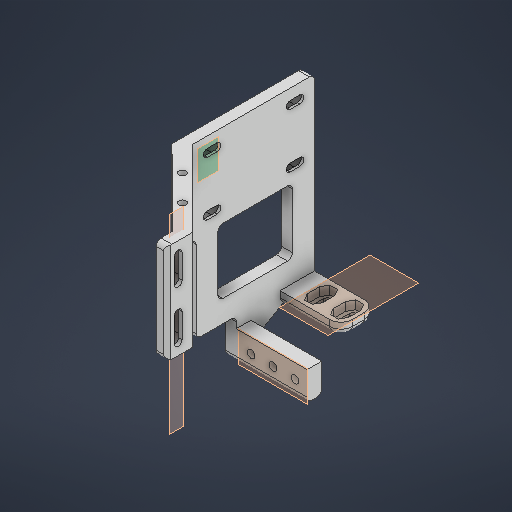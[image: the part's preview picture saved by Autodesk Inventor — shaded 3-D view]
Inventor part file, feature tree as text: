
AUTODESK INVENTOR PART (.ipt)
format: ipt  version: 2025 (Build 290162000, 162)  size: 845,824 bytes
history: native  units: mm
features: reference x38, extrude x24, sketch x21, other x9, plane x7, fillet x7, projected_geometry x5, chamfer x3, loft x1
ambient origin geometry x8: Origin, YZ Plane, XZ Plane, XY Plane, X Axis, Y Axis, Z Axis, Center Point
bodies: Solid1 (feature_tree)
feature tree (115):
  plane  "Work Plane1"
  extrude  "Extrusion1"  Depth=4.5mm TaperAngle=0.0deg
  plane  "Work Plane2"
  extrude  "Extrusion2"  Depth=2.0mm
  extrude  "Extrusion4"  Depth=3.2mm
  extrude  "Extrusion5"  Depth=6.0mm
  sketch  "Sketch7"  dims[d22=6.0mm d23=6.0mm]
  plane  "Work Plane3"
  extrude  "Extrusion6"  Depth=6.0mm
  plane  "Work Plane4"
  extrude  "Extrusion7"  Depth=6.0mm TaperAngle=0.0deg
  extrude  "Extrusion8"  Depth=6.0mm
  sketch  "Sketch10"  dims[d31=6.0mm d32=6.0mm]
  plane  "Work Plane5"
  extrude  "Extrusion9"  Depth=6.0mm
  extrude  "Extrusion10"  Depth=4.5mm
  loft  "Loft3"
  extrude  "Extrusion11"  Depth=10.58mm
  extrude  "Extrusion12"  Depth=3.0mm
  extrude  "Extrusion13"  Depth=4.5mm TaperAngle=0.0deg
  sketch  "Sketch15"  dims[d51=4.5mm d52=0.0mm d53=4.5mm d54=0.0mm]
  plane  "Work Plane6"
  extrude  "Extrusion14"  Depth=10.0mm
  fillet  "Fillet3"  Radius=24.197245mm
  sketch  "Sketch16"  dims[d55=10.0mm d56=0.0mm d57=7.218682mm d58=24.197245mm]
  extrude  "Extrusion15"  TaperAngle=0.0deg  [1 undecoded]
  extrude  "Extrusion16"  Depth=1.893mm
  extrude  "Extrusion17"  Depth=10.0mm TaperAngle=0.0deg
  extrude  "Extrusion18"  Depth=3.2mm
  chamfer  "Chamfer2"  Distance=3.2mm
  chamfer  "Chamfer3"  Distance=6.0mm
  fillet  "Fillet4"  Radius=6.0mm
  extrude  "Extrusion20"  Depth=6.0mm
  chamfer  "Chamfer4"  Distance=6.0mm
  sketch  "Sketch20"  dims[d66=10.0mm d67=0.0mm d68=10.0mm d69=0.0mm]
  extrude  "Extrusion21"  Depth=6.0mm
  extrude  "Extrusion22"  Depth=6.0mm
  fillet  "Fillet5"  Radius=3.0mm
  extrude  "Extrusion23"  Depth=10.0mm TaperAngle=0.0deg
  extrude  "Extrusion24"  Depth=9.0mm
  fillet  "Fillet6"  Radius=2.0mm
  fillet  "Fillet7"  Radius=1.5mm
  plane  "Work Plane8"
  extrude  "Extrusion27"  Depth=2.0mm
  extrude  "Extrusion28"  Depth=10.0mm
  fillet  "Fillet11"  Radius=3.2mm
  fillet  "Fillet12"  Radius=10.0mm
  sketch  "Sketch1"  dims[d0=4.5mm d1=0.0mm d2=4.5mm d3=0.0mm]
  reference  "Reference1"
  reference  "Reference2"
  reference  "Reference3"
  reference  "Reference4"
  reference  "Reference5"
  reference  "Reference6"
  reference  "Reference7"
  reference  "Reference8"
  reference  "Reference9"
  reference  "Reference10"
  reference  "Reference11"
  reference  "Reference12"
  reference  "Reference13"
  reference  "Reference14"
  reference  "Reference15"
  reference  "Reference16"
  reference  "Reference17"
  reference  "Reference18"
  reference  "Reference19"
  reference  "Reference20"
  sketch  "Sketch2"  dims[d8=2.0mm d17=3.2mm]
  reference  "Reference21"
  reference  "Reference22"
  reference  "Reference23"
  reference  "Reference24"
  reference  "Reference31"
  reference  "Reference32"
  reference  "Reference33"
  reference  "Reference34"
  sketch  "Sketch4"  dims[d18=3.2mm d19=3.2mm]
  sketch  "Sketch6"  dims[d20=3.2mm d21=6.0mm]
  projected_geometry  "Projected Loop1"
  sketch  "Sketch8"  dims[d24=6.0mm d25=3.5mm d26=0.0mm]
  reference  "Reference35"
  reference  "Reference36"
  reference  "Reference37"
  sketch  "Sketch9"  dims[d29=6.0mm d30=6.0mm]
  projected_geometry  "Projected Loop2"
  sketch  "Sketch11"  dims[d39=4.5mm d40=0.0mm d41=15.0mm]
  other  "Edges4"
  other  "Edges5"
  sketch  "Sketch12"  dims[d42=10.0mm d43=0.0mm d44=10.58mm]
  sketch  "Sketch13"  dims[d45=5.29mm d46=10.58mm]
  reference  "Reference38"
  reference  "Reference39"
  reference  "Reference40"
  sketch  "Sketch14"  dims[d47=3.0mm d48=3.0mm]
  reference  "Reference41"
  sketch  "Sketch17"  dims[d59=10.0mm d60=0.0mm d61=0.0mm d62=90.0deg]
  projected_geometry  "Projected Loop3"
  sketch  "Sketch19"  dims[d63=0.0mm d64=90.0deg d65=1.893mm]
  projected_geometry  "Projected Loop4"
  sketch  "Sketch21"  dims[d72=3.2mm d73=3.2mm]
  sketch  "Sketch22"  dims[d74=4.0mm]
  sketch  "Sketch25"  dims[d75=3.2mm]
  reference  "Reference45"
  reference  "Reference46"
  reference  "Reference47"
  sketch  "Sketch26"  dims[d76=4.0mm d77=3.2mm d78=6.0mm d79=6.0mm d80=6.0mm d81=6.0mm d82=6.0mm d83=6.0mm d84=3.0mm d85=0.0mm d93=10.0mm d94=0.0mm d96=9.0mm d97=2.0mm d98=1.5mm d100=1.5mm d102=10.0mm d103=3.2mm d104=10.0mm d105=3.2mm d106=3.0mm d107=0.0mm d108=3.0mm d109=3.0mm d110=3.0mm d111=0.0mm d112=3.0mm d113=0.0mm d114=10.0mm d115=0.0mm d116=3.0mm d117=2.0mm d118=45.0deg d123=1.5mm d124=2.0mm d125=45.0deg d126=2.0mm d127=3.0mm d128=0.0mm d129=3.0mm d130=2.0mm d131=45.0deg d132=6.0mm d133=6.0mm d134=3.0mm d135=0.0mm d136=9.0mm d137=7.5mm d138=7.5mm d139=3.0mm d140=3.0mm d141=8.0mm d142=0.0mm d143=2.0mm d144=6.0mm d145=3.0mm d146=0.0mm d147=5.0mm d148=3.2mm d149=5.0mm d150=3.2mm d151=3.0mm d152=3.0mm d153=2.725mm d154=2.725mm d155=3.5mm d156=0.0mm d157=2.725mm d158=2.0mm d159=2.0mm d168=28.0mm d169=3.1mm d170=3.1mm d171=3.1mm d172=6.0mm d173=0.0mm d174=4.5mm d175=0.0mm d176=2.0mm d177=2.0mm]
  projected_geometry  "Projected Loop5"
  other  "<userpath> 7 was better\GitHub\ReplicatorPlusConversion\CAD\Inventor\hotend-new.iam"
  other  "hotend-new.iam"
  other  "bolts reference:1"
  other  "Hemera_XS_Reference_CAD:1"
  other  "eddy:2"
  other  "hemera-xs-duct-mount-v2:1"
  other  "BL-touch:1"
note: 1 required parameter value undecoded (feature->parameter linkage not recoverable at this tier; creation-order binding heuristic only, values carry confidence <= 0.55)
